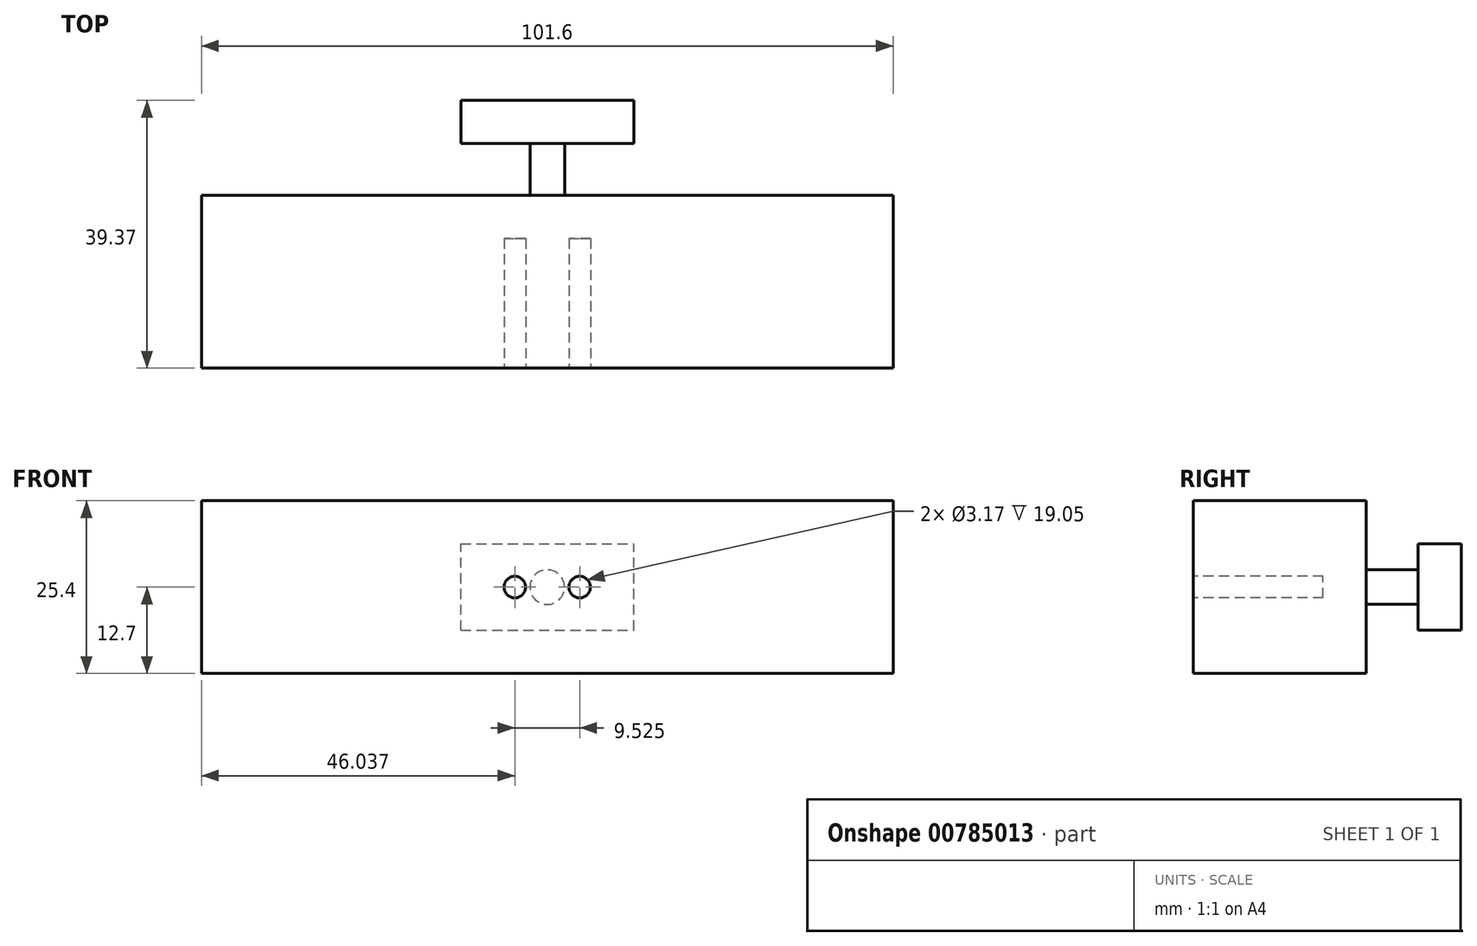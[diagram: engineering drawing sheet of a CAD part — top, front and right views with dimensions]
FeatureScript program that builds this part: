
annotation { "Feature Type Name" : "Feature", "Feature Type Description" : "" }
export const myFeature = defineFeature(function(context is Context, id is Id, definition is map)
    precondition{}
    {
        {
            var Q0;
            Q0=qCreatedBy(makeId("Front.planeOp"),FACE);
            var sketch = newSketch(context, id + "F0", { "sketchPlane" : qUnion([Q0])});
            skLineSegment(sketch, "E0.bottom", {"start": v(50.8, -12.7) * mm, "end": v(-50.8, -12.7) * mm});
            skLineSegment(sketch, "E0.top", {"start": v(50.8, 12.7) * mm, "end": v(-50.8, 12.7) * mm});
            skLineSegment(sketch, "E0.left", {"start": v(50.8, -12.7) * mm, "end": v(50.8, 12.7) * mm});
            skLineSegment(sketch, "E0.right", {"start": v(-50.8, -12.7) * mm, "end": v(-50.8, 12.7) * mm});
            skPoint(sketch, "E0.middle", {"position": v(0, 0) * mm});
            skCircle(sketch, "E1", {"center": v(4.76, 0) * mm, "radius": 1.59 * mm});
            skCircle(sketch, "E2", {"center": v(-4.76, 0) * mm, "radius": 1.59 * mm});
            skSolve(sketch);
        }
        {
            var Q0;
            Q0=qSketchRegion(id+"F0",true);
            var Q1;
            Q1=makeQuery(id+"F0.imprint","IMPRINT",FACE,{"disambiguationData":[TD([[makeQuery(id+"F0.imprint","IMPRINT",EDGE,{"derivedFrom":sQuery(id+"F0.wireOp",EDGE,"E1")}),1.0]])]});
            var Q2;
            Q2=makeQuery(id+"F0.imprint","IMPRINT",FACE,{"disambiguationData":[TD([[makeQuery(id+"F0.imprint","IMPRINT",EDGE,{"derivedFrom":sQuery(id+"F0.wireOp",EDGE,"E2")}),1.0]])]});
            extrude(context, id + "F1", {"entities" : qUnion([Q0, Q1, Q2]), "oppositeDirection" : true, "depth" : 25.4 * mm, "offsetDistance" : 25.4 * mm});
        }
        {
            var Q0;
            Q0=makeQuery(id+"F1.opExtrude","CAP_FACE",FACE,{"disambiguationData":[OSD([sQuery(id+"F0.wireOp",EDGE,"E0.bottom"),sQuery(id+"F0.wireOp",EDGE,"E0.top"),sQuery(id+"F0.wireOp",EDGE,"E0.left"),sQuery(id+"F0.wireOp",EDGE,"E0.right")])],"isStart":false});
            var sketch = newSketch(context, id + "F2", { "sketchPlane" : qUnion([Q0])});
            skCircle(sketch, "E3", {"center": v(0, 0) * mm, "radius": 2.54 * mm});
            skSolve(sketch);
        }
        {
            var Q0;
            Q0=makeQuery(id+"F2.imprint","IMPRINT",FACE,{"disambiguationData":[TD([[makeQuery(id+"F2.imprint","IMPRINT",EDGE,{"derivedFrom":sQuery(id+"F2.wireOp",EDGE,"E3")}),1.0]])]});
            extrude(context, id + "F3", {"entities" : qUnion([Q0]), "operationType" : NewBodyOperationType.ADD, "depth" : 7.62 * mm, "offsetDistance" : 25.4 * mm});
        }
        {
            var Q0;
            Q0=makeQuery(id+"F3.opExtrude","CAP_FACE",FACE,{"disambiguationData":[OSD([sQuery(id+"F2.wireOp",EDGE,"E3")])],"isStart":false});
            var sketch = newSketch(context, id + "F4", { "sketchPlane" : qUnion([Q0])});
            skLineSegment(sketch, "E4.bottom", {"start": v(12.7, -6.35) * mm, "end": v(-12.7, -6.35) * mm});
            skLineSegment(sketch, "E4.top", {"start": v(12.7, 6.35) * mm, "end": v(-12.7, 6.35) * mm});
            skLineSegment(sketch, "E4.left", {"start": v(12.7, -6.35) * mm, "end": v(12.7, 6.35) * mm});
            skLineSegment(sketch, "E4.right", {"start": v(-12.7, -6.35) * mm, "end": v(-12.7, 6.35) * mm});
            skPoint(sketch, "E4.middle", {"position": v(0, 0) * mm});
            skSolve(sketch);
        }
        {
            var Q0;
            Q0=qSketchRegion(id+"F4",true);
            extrude(context, id + "F5", {"entities" : qUnion([Q0]), "operationType" : NewBodyOperationType.ADD, "depth" : 6.35 * mm, "offsetDistance" : 25.4 * mm});
        }
        {
            var Q0;
            Q0=makeQuery(id+"F0.imprint","IMPRINT",FACE,{"disambiguationData":[TD([[makeQuery(id+"F0.imprint","IMPRINT",EDGE,{"derivedFrom":sQuery(id+"F0.wireOp",EDGE,"E2")}),1.0]])]});
            var Q1;
            Q1=makeQuery(id+"F0.imprint","IMPRINT",FACE,{"disambiguationData":[TD([[makeQuery(id+"F0.imprint","IMPRINT",EDGE,{"derivedFrom":sQuery(id+"F0.wireOp",EDGE,"E1")}),1.0]])]});
            extrude(context, id + "F6", {"entities" : qUnion([Q0, Q1]), "operationType" : NewBodyOperationType.REMOVE, "oppositeDirection" : true, "depth" : 19.05 * mm, "offsetDistance" : 25.4 * mm});
        }
    });
